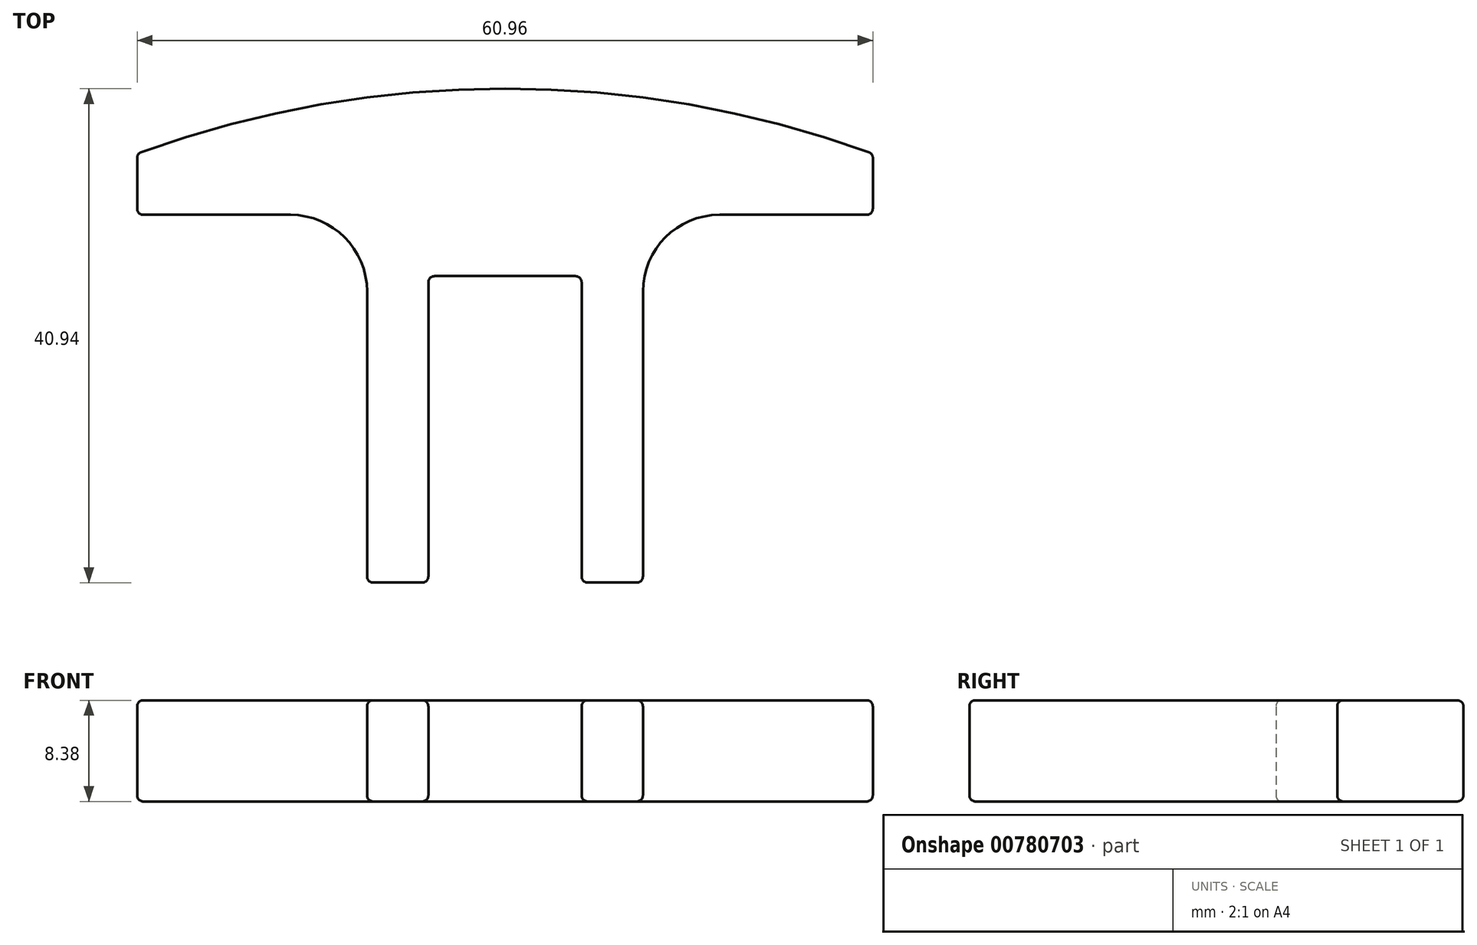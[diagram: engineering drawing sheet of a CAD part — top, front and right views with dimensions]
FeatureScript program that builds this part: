
annotation { "Feature Type Name" : "Feature", "Feature Type Description" : "" }
export const myFeature = defineFeature(function(context is Context, id is Id, definition is map)
    precondition{}
    {
        {
            var Q0;
            Q0=qCreatedBy(makeId("Top.planeOp"),FACE);
            var sketch = newSketch(context, id + "F0", { "sketchPlane" : qUnion([Q0])});
            skLineSegment(sketch, "E0", {"start": v(-16.82, 4.57) * mm, "end": v(-16.82, 28.7) * mm});
            skLineSegment(sketch, "E1", {"start": v(-16.82, 35.05) * mm, "end": v(6.04, 35.05) * mm});
            skLineSegment(sketch, "E2", {"start": v(6.04, 28.7) * mm, "end": v(6.04, 4.57) * mm});
            skLineSegment(sketch, "E3", {"start": v(6.04, 4.57) * mm, "end": v(0.96, 4.57) * mm});
            skLineSegment(sketch, "E4", {"start": v(0.96, 4.57) * mm, "end": v(0.96, 29.97) * mm});
            skLineSegment(sketch, "E5", {"start": v(0.96, 29.97) * mm, "end": v(-11.74, 29.97) * mm});
            skLineSegment(sketch, "E6", {"start": v(-11.74, 29.97) * mm, "end": v(-11.74, 4.57) * mm});
            skLineSegment(sketch, "E7", {"start": v(-11.74, 4.57) * mm, "end": v(-16.82, 4.57) * mm});
            skLineSegment(sketch, "E8", {"start": v(12.4, 35.05) * mm, "end": v(25.1, 35.05) * mm});
            skLineSegment(sketch, "E9", {"start": v(25.1, 35.05) * mm, "end": v(25.1, 40.13) * mm});
            skLineSegment(sketch, "E10", {"start": v(-23.17, 35.05) * mm, "end": v(-35.87, 35.05) * mm});
            skLineSegment(sketch, "E11", {"start": v(-35.87, 35.05) * mm, "end": v(-35.87, 40.13) * mm});
            skArc(sketch, "E12", {"start": v(25.1, 40.13) * mm, "mid": v(-5.39, 45.51) * mm, "end": v(-35.87, 40.13) * mm});
            skPoint(sketch, "E13.visualSharp", {"position": v(6.04, 35.05) * mm});
            skArc(sketch, "E13.filletArc", {"start": v(12.4, 35.05) * mm, "mid": v(7.9, 33.2) * mm, "end": v(6.04, 28.7) * mm});
            skPoint(sketch, "E14.visualSharp", {"position": v(-16.82, 35.05) * mm});
            skArc(sketch, "E14.filletArc", {"start": v(-16.82, 28.7) * mm, "mid": v(-18.68, 33.2) * mm, "end": v(-23.17, 35.05) * mm});
            skSolve(sketch);
        }
        {
            var Q0;
            Q0=makeQuery(id+"F0.imprint","IMPRINT",FACE,{"disambiguationData":[TD([[makeQuery(id+"F0.imprint","IMPRINT",EDGE,{"derivedFrom":sQuery(id+"F0.wireOp",EDGE,"E1")}),1.0]])]});
            var Q1;
            Q1=makeQuery(id+"F0.imprint","IMPRINT",FACE,{"disambiguationData":[TD([[makeQuery(id+"F0.imprint","IMPRINT",EDGE,{"derivedFrom":sQuery(id+"F0.wireOp",EDGE,"E0")}),-1.0]])]});
            extrude(context, id + "F1", {"entities" : qUnion([Q0, Q1]), "depth" : 8.38 * mm, "offsetDistance" : 25.4 * mm});
        }
        {
            var Q0;
            Q0=makeQuery(id+"F1.opExtrude","CAP_EDGE",EDGE,{"disambiguationData":[OSD([sQuery(id+"F0.wireOp",EDGE,"E2")])],"isStart":false});
            var Q1;
            Q1=makeQuery(id+"F1.opExtrude","CAP_EDGE",EDGE,{"disambiguationData":[OSD([sQuery(id+"F0.wireOp",EDGE,"E3")])],"isStart":false});
            var Q2;
            Q2=makeQuery(id+"F1.opExtrude","CAP_FACE",FACE,{"disambiguationData":[OSD([sQuery(id+"F0.wireOp",EDGE,"E0"),sQuery(id+"F0.wireOp",EDGE,"E2"),sQuery(id+"F0.wireOp",EDGE,"E3"),sQuery(id+"F0.wireOp",EDGE,"E4"),sQuery(id+"F0.wireOp",EDGE,"E5"),sQuery(id+"F0.wireOp",EDGE,"E6"),sQuery(id+"F0.wireOp",EDGE,"E7"),sQuery(id+"F0.wireOp",EDGE,"E8"),sQuery(id+"F0.wireOp",EDGE,"E9"),sQuery(id+"F0.wireOp",EDGE,"E10"),sQuery(id+"F0.wireOp",EDGE,"E11"),sQuery(id+"F0.wireOp",EDGE,"E12")])],"isStart":false});
            var Q3;
            Q3=makeQuery(id+"F1.opExtrude","CAP_EDGE",EDGE,{"disambiguationData":[OSD([sQuery(id+"F0.wireOp",EDGE,"E12")])],"isStart":true});
            var Q4;
            Q4=makeQuery(id+"F1.opExtrude","CAP_EDGE",EDGE,{"disambiguationData":[OSD([sQuery(id+"F0.wireOp",EDGE,"E9")])],"isStart":true});
            var Q5;
            Q5=makeQuery(id+"F1.opExtrude","CAP_EDGE",EDGE,{"disambiguationData":[OSD([sQuery(id+"F0.wireOp",EDGE,"E8")])],"isStart":true});
            var Q6;
            Q6=makeQuery(id+"F1.opExtrude","CAP_FACE",FACE,{"disambiguationData":[OSD([sQuery(id+"F0.wireOp",EDGE,"E0"),sQuery(id+"F0.wireOp",EDGE,"E2"),sQuery(id+"F0.wireOp",EDGE,"E3"),sQuery(id+"F0.wireOp",EDGE,"E4"),sQuery(id+"F0.wireOp",EDGE,"E5"),sQuery(id+"F0.wireOp",EDGE,"E6"),sQuery(id+"F0.wireOp",EDGE,"E7"),sQuery(id+"F0.wireOp",EDGE,"E8"),sQuery(id+"F0.wireOp",EDGE,"E9"),sQuery(id+"F0.wireOp",EDGE,"E10"),sQuery(id+"F0.wireOp",EDGE,"E11"),sQuery(id+"F0.wireOp",EDGE,"E12")])],"isStart":true});
            var Q7;
            Q7=makeQuery(id+"F1.opExtrude","SWEPT_FACE",FACE,{"disambiguationData":[OSD([sQuery(id+"F0.wireOp",EDGE,"E12")])]});
            var Q8;
            Q8=makeQuery(id+"F1.opExtrude","SWEPT_FACE",FACE,{"disambiguationData":[OSD([sQuery(id+"F0.wireOp",EDGE,"E8")])]});
            var Q9;
            Q9=makeQuery(id+"F1.opExtrude","SWEPT_FACE",FACE,{"disambiguationData":[OSD([sQuery(id+"F0.wireOp",EDGE,"E2")])]});
            var Q10;
            Q10=makeQuery(id+"F1.opExtrude","SWEPT_FACE",FACE,{"disambiguationData":[OSD([sQuery(id+"F0.wireOp",EDGE,"E4")])]});
            var Q11;
            Q11=makeQuery(id+"F1.opExtrude","SWEPT_FACE",FACE,{"disambiguationData":[OSD([sQuery(id+"F0.wireOp",EDGE,"E6")])]});
            var Q12;
            Q12=makeQuery(id+"F1.opExtrude","SWEPT_FACE",FACE,{"disambiguationData":[OSD([sQuery(id+"F0.wireOp",EDGE,"E7")])]});
            var Q13;
            Q13=makeQuery(id+"F1.opExtrude","SWEPT_FACE",FACE,{"disambiguationData":[OSD([sQuery(id+"F0.wireOp",EDGE,"E0")])]});
            var Q14;
            Q14=makeQuery(id+"F1.opExtrude","SWEPT_FACE",FACE,{"disambiguationData":[OSD([sQuery(id+"F0.wireOp",EDGE,"E10")])]});
            fillet(context, id + "F2", {"entities" : qUnion([Q0, Q1, Q2, Q3, Q4, Q5, Q6, Q7, Q8, Q9, Q10, Q11, Q12, Q13, Q14]), "radius" : 0.5 * mm, "tangentPropagation" : true, "allowEdgeOverflow" : false});
        }
    });
